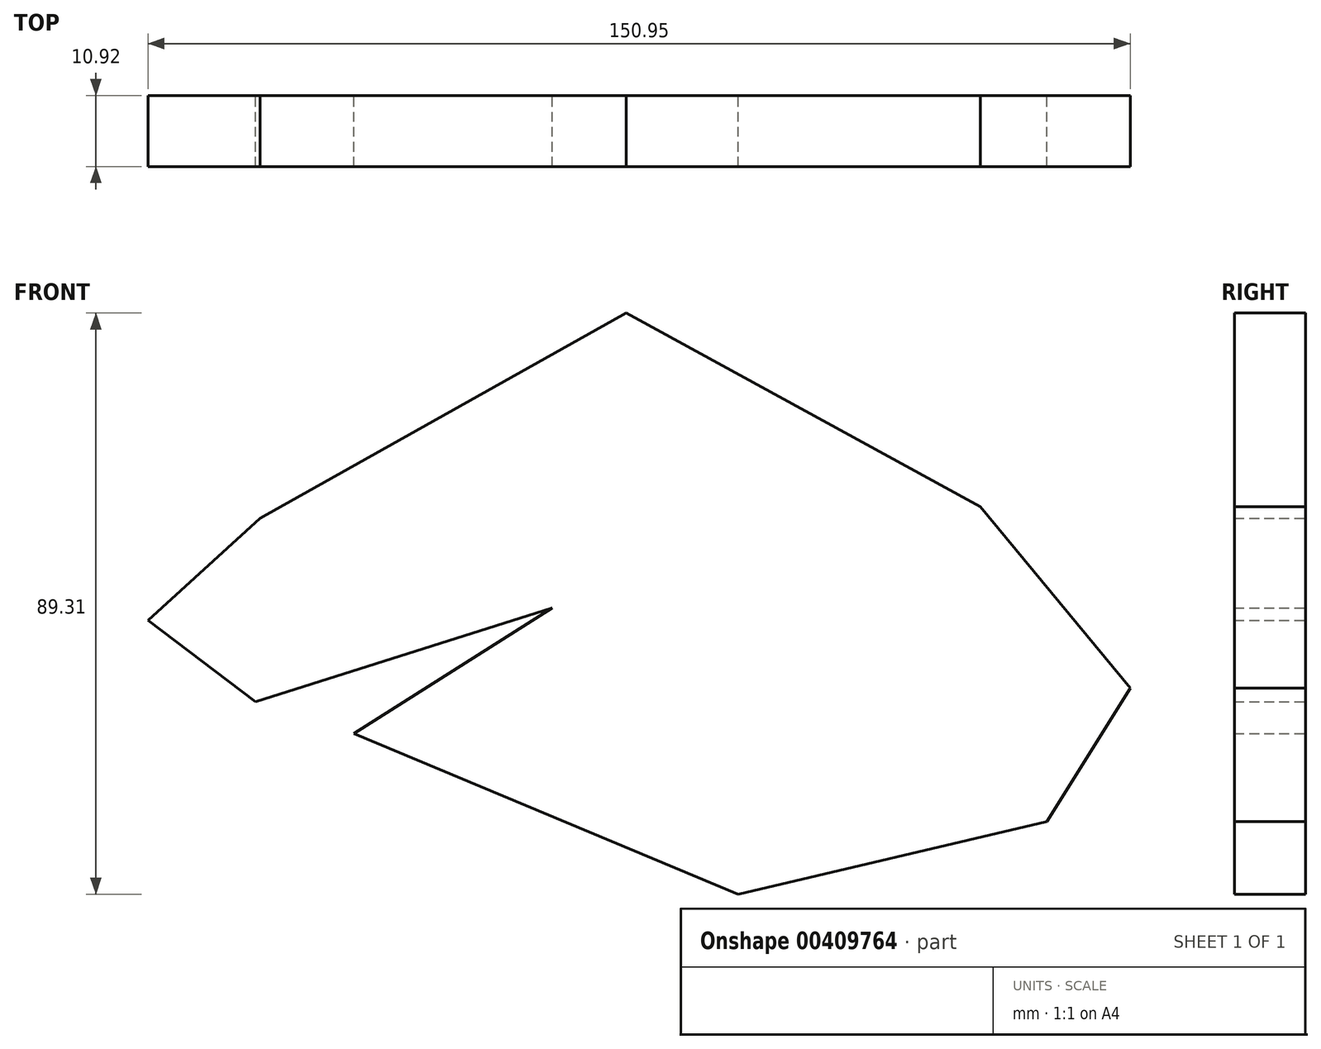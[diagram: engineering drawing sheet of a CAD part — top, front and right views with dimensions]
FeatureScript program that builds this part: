
annotation { "Feature Type Name" : "Feature", "Feature Type Description" : "" }
export const myFeature = defineFeature(function(context is Context, id is Id, definition is map)
    precondition{}
    {
        {
            var Q0;
            Q0=qCreatedBy(makeId("Front.planeOp"),FACE);
            var sketch = newSketch(context, id + "F0", { "sketchPlane" : qUnion([Q0])});
            skLineSegment(sketch, "E0", {"start": v(-72.57, 6.75) * mm, "end": v(-15.35, 38.84) * mm});
            skLineSegment(sketch, "E1", {"start": v(-15.35, 38.84) * mm, "end": v(39.07, 9.07) * mm});
            skLineSegment(sketch, "E2", {"start": v(39.07, 9.07) * mm, "end": v(62.1, -18.84) * mm});
            skLineSegment(sketch, "E3", {"start": v(62.1, -18.84) * mm, "end": v(49.3, -39.3) * mm});
            skLineSegment(sketch, "E4", {"start": v(49.3, -39.3) * mm, "end": v(1.86, -50.47) * mm});
            skLineSegment(sketch, "E5", {"start": v(1.86, -50.47) * mm, "end": v(-57.22, -25.82) * mm});
            skLineSegment(sketch, "E6", {"start": v(-57.22, -25.82) * mm, "end": v(-26.75, -6.51) * mm});
            skLineSegment(sketch, "E7", {"start": v(-26.75, -6.51) * mm, "end": v(-72.33, -20.93) * mm});
            skLineSegment(sketch, "E8", {"start": v(-72.33, -20.93) * mm, "end": v(-88.85, -8.37) * mm});
            skLineSegment(sketch, "E9", {"start": v(-88.85, -8.37) * mm, "end": v(-71.6, 7.29) * mm});
            skSolve(sketch);
        }
        {
            var Q0;
            {var subQ0=sQuery(id+"F0.wireOp",EDGE,"E1");Q0=makeQuery(id+"F0.imprint","IMPRINT",FACE,{"disambiguationData":[TD([[makeQuery(id+"F0.imprint","IMPRINT",EDGE,{"derivedFrom":subQ0}),-1.0]])]});}
            extrude(context, id + "F1", {"entities" : qUnion([Q0]), "depth" : 10.92 * mm});
        }
    });
